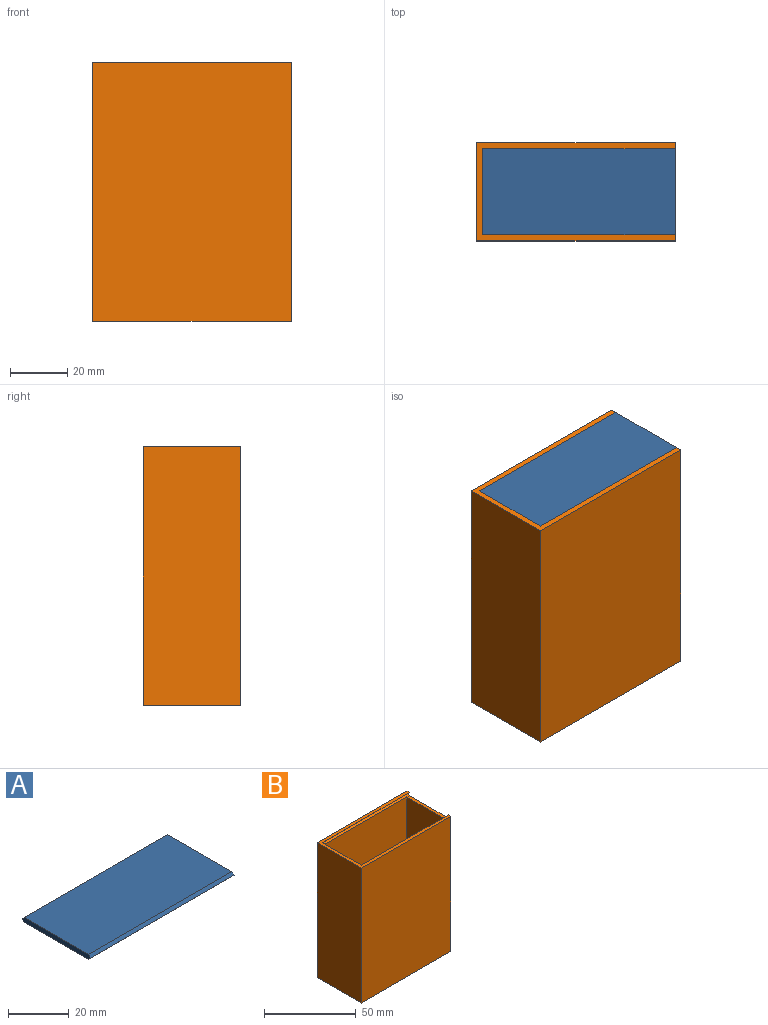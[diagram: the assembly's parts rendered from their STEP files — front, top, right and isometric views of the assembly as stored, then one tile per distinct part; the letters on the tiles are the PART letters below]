
ASSEMBLY  parts=2 mates=1
PART A: 8 faces, bbox 67x32x2 mm
  f0: plane 32x2mm, normal (1,0,0), area 62mm2, adj f2,f3,f4,f5,f6,f7
  f1: plane 32x2mm, normal (-1,0,0), area 62mm2, adj f2,f3,f4,f5,f6,f7
  f2: plane 67x30mm, normal (0,0,1), area 2010mm2, adj f0,f1,f4,f6
  f3: plane 67x30mm, normal (0,0,-1), area 2010mm2, adj f0,f1,f5,f7
  f4: plane 67x1mm, normal (0,0.71,0.71), area 94.8mm2, adj f0,f1,f2,f5
  f5: plane 67x1mm, normal (0,0.71,-0.71), area 94.8mm2, adj f0,f1,f3,f4
  f6: plane 67x1mm, normal (0,-0.71,0.71), area 94.8mm2, adj f0,f1,f2,f7
  f7: plane 67x1mm, normal (0,-0.71,-0.71), area 94.8mm2, adj f0,f1,f3,f6
PART B: 16 faces, bbox 69x34x90 mm
  f0: plane 90x34mm, normal (1,0,0), area 2998mm2, adj f1,f3,f4,f6,f11,f12,f13,f14
  f1: plane 69x34mm, normal (0,0,1), area 336mm2, adj f0,f3,f4,f5,f9,f12,f14
  f2: plane 86x30mm, normal (-1,0,0), area 2580mm2, adj f7,f8,f10,f11
  f3: plane 90x69mm, normal (0,-1,0), area 6210mm2, adj f0,f1,f5,f6
  f4: plane 90x69mm, normal (0,1,0), area 6210mm2, adj f0,f1,f5,f6
  f5: plane 90x34mm, normal (-1,0,0), area 3060mm2, adj f1,f3,f4,f6
  f6: plane 69x34mm, normal (0,0,-1), area 2346mm2, adj f0,f3,f4,f5
  f7: plane 86x65mm, normal (0,1,0), area 5590mm2, adj f2,f9,f10,f15
  f8: plane 86x65mm, normal (0,-1,0), area 5590mm2, adj f2,f9,f10,f13
  f9: plane 88x32mm, normal (1,0,0), area 2642mm2, adj f1,f7,f8,f10,f12,f13,f14,f15
  f10: plane 65x30mm, normal (0,0,1), area 1950mm2, adj f2,f7,f8,f9
  f11: plane 30x2mm, normal (0,0,1), area 60mm2, adj f0,f2,f13,f15
  f12: plane 67x1mm, normal (0,-0.71,-0.71), area 94.8mm2, adj f0,f1,f9,f13
  f13: plane 67x1mm, normal (0,-0.71,0.71), area 94.8mm2, adj f0,f8,f9,f11,f12
  f14: plane 67x1mm, normal (0,0.71,-0.71), area 94.8mm2, adj f0,f1,f9,f15
  f15: plane 67x1mm, normal (0,0.71,0.71), area 94.8mm2, adj f0,f7,f9,f11,f14
PLACE A t=(1,0,88)mm
PLACE B at identity
MATE fastened A.f1 <-> B.f9  axis (-1,0,0) through (-32.5,0,90)mm
